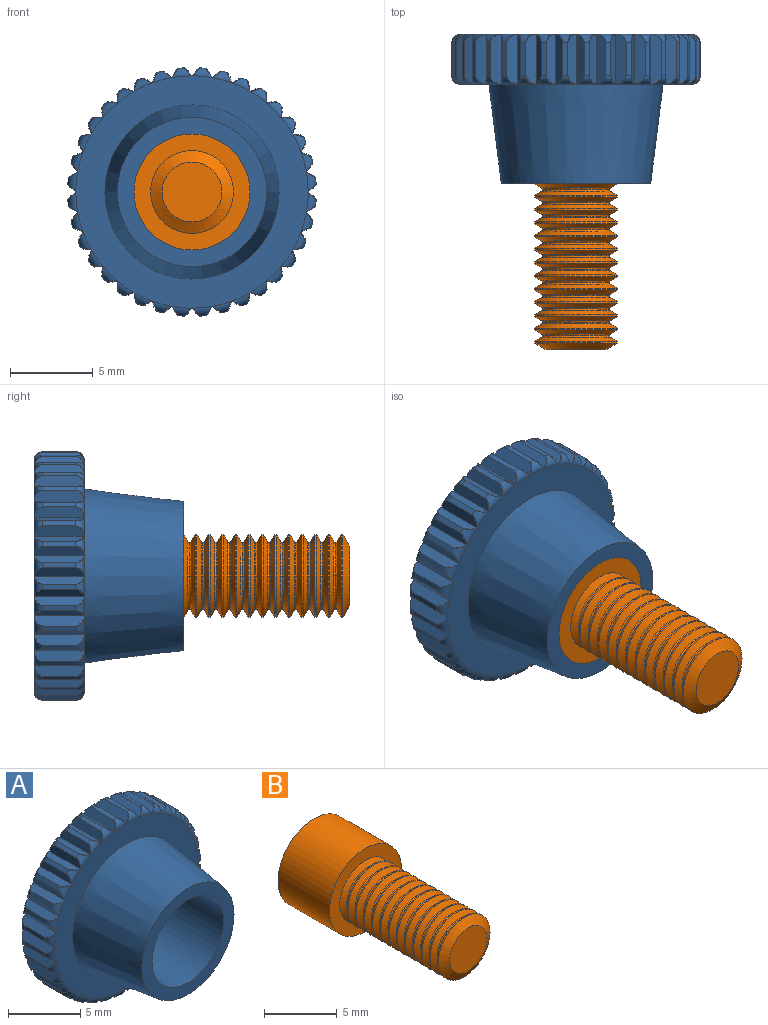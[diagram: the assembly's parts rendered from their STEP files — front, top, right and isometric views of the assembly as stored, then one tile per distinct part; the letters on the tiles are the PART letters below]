
ASSEMBLY  parts=2 mates=1
PART A: 188 faces, bbox 15.2x9.2x15.2 mm
  f0: plane 10.5x10.5mm, normal (0,1,0), area 86.6mm2, adj f1
  f1: cylinder r=5.25mm len=10.5mm, axis (0,-1,0), area 9.9mm2, adj f0,f2
  f2: plane 14x14mm, normal (0,1,0), area 67.3mm2, adj f1,f3,f4,f5,f6,f7,f8,f9
  f3: torus R=7mm, axis (0,1,0), area 0.6mm2, adj f2,f39,f40,f41
  f4: torus R=7mm, axis (0,1,0), area 0.6mm2, adj f2,f42,f43,f44
  f5: torus R=7mm, axis (0,1,0), area 0.6mm2, adj f2,f45,f46,f47
  f6: torus R=7mm, axis (0,1,0), area 0.6mm2, adj f2,f48,f49,f50
  f7: torus R=7mm, axis (0,1,0), area 0.6mm2, adj f2,f51,f52,f53
  f8: torus R=7mm, axis (0,1,0), area 0.6mm2, adj f2,f54,f55,f56
  f9: torus R=7mm, axis (0,1,0), area 0.6mm2, adj f2,f57,f58,f59
  f10: torus R=7mm, axis (0,1,0), area 0.6mm2, adj f2,f60,f61,f62
  f11: torus R=7mm, axis (0,1,0), area 0.6mm2, adj f2,f63,f64,f65
  f12: torus R=7mm, axis (0,1,0), area 0.6mm2, adj f2,f66,f67,f68
  f13: torus R=7mm, axis (0,1,0), area 0.6mm2, adj f2,f69,f70,f71
  f14: torus R=7mm, axis (0,1,0), area 0.6mm2, adj f2,f72,f73,f74
  f15: torus R=7mm, axis (0,1,0), area 0.6mm2, adj f2,f75,f76,f77
  f16: torus R=7mm, axis (0,1,0), area 0.6mm2, adj f2,f78,f79,f80
  f17: torus R=7mm, axis (0,1,0), area 0.6mm2, adj f2,f81,f82,f83
  f18: torus R=7mm, axis (0,1,0), area 0.6mm2, adj f2,f84,f85,f86
  f19: torus R=7mm, axis (0,1,0), area 0.6mm2, adj f2,f87,f88,f89
  f20: torus R=7mm, axis (0,1,0), area 0.6mm2, adj f2,f90,f91,f92
  f21: torus R=7mm, axis (0,1,0), area 0.6mm2, adj f2,f93,f94,f95
  f22: torus R=7mm, axis (0,1,0), area 0.6mm2, adj f2,f96,f97,f98
  f23: torus R=7mm, axis (0,1,0), area 0.6mm2, adj f2,f99,f100,f101
  f24: torus R=7mm, axis (0,1,0), area 0.6mm2, adj f2,f102,f103,f104
  f25: torus R=7mm, axis (0,1,0), area 0.6mm2, adj f2,f105,f106,f107
  f26: torus R=7mm, axis (0,1,0), area 0.6mm2, adj f2,f108,f109,f110
  f27: torus R=7mm, axis (0,1,0), area 0.6mm2, adj f2,f111,f112,f113
  f28: torus R=7mm, axis (0,1,0), area 0.6mm2, adj f2,f114,f115,f116
  f29: torus R=7mm, axis (0,1,0), area 0.6mm2, adj f2,f117,f118,f119
  f30: torus R=7mm, axis (0,1,0), area 0.6mm2, adj f2,f120,f121,f122
  f31: torus R=7mm, axis (0,1,0), area 0.6mm2, adj f2,f123,f124,f125
  f32: torus R=7mm, axis (0,1,0), area 0.6mm2, adj f2,f126,f127,f128
  f33: torus R=7mm, axis (0,1,0), area 0.6mm2, adj f2,f129,f130,f131
  f34: torus R=7mm, axis (0,1,0), area 0.6mm2, adj f2,f132,f133,f134
  f35: torus R=7mm, axis (0,1,0), area 0.6mm2, adj f2,f135,f136,f137
  f36: torus R=7mm, axis (0,1,0), area 0.6mm2, adj f2,f138,f139,f140
  f37: torus R=7mm, axis (0,1,0), area 0.6mm2, adj f2,f141,f142,f143
  f38: torus R=7mm, axis (0,1,0), area 0.6mm2, adj f2,f144,f145,f146
  f39: plane 3.19x0.75mm, normal (-0.57,0,-0.82), area 1.9mm2, adj f3,f41,f42,f147
  f40: plane 3.19x0.67mm, normal (-0.71,0,0.71), area 1.9mm2, adj f3,f41,f146,f147
  f41: cylinder r=7.5mm len=2mm, axis (0,-1,0), area 0.7mm2, adj f3,f39,f40,f147
  f42: plane 3.19x0.75mm, normal (-0.82,0,0.57), area 1.9mm2, adj f4,f39,f43,f148
  f43: cylinder r=7.5mm len=2mm, axis (0,-1,0), area 0.7mm2, adj f4,f42,f44,f148
  f44: plane 3.19x0.81mm, normal (-0.42,0,-0.91), area 1.9mm2, adj f4,f43,f45,f148
  f45: plane 3.19x0.81mm, normal (-0.91,0,0.42), area 1.9mm2, adj f5,f44,f46,f149
  f46: cylinder r=7.5mm len=2mm, axis (0,-1,0), area 0.7mm2, adj f5,f45,f47,f149
  f47: plane 3.19x0.85mm, normal (-0.26,0,-0.97), area 1.9mm2, adj f5,f46,f48,f149
  f48: plane 3.19x0.85mm, normal (-0.97,0,0.26), area 1.9mm2, adj f6,f47,f49,f150
  f49: cylinder r=7.5mm len=2mm, axis (0,-1,0), area 0.7mm2, adj f6,f48,f50,f150
  f50: plane 3.19x0.87mm, normal (-0.09,0,-1), area 1.9mm2, adj f6,f49,f51,f150
  f51: plane 3.19x0.87mm, normal (-1,0,0.09), area 1.9mm2, adj f7,f50,f52,f151
  f52: cylinder r=7.5mm len=2mm, axis (0,-1,0), area 0.7mm2, adj f7,f51,f53,f151
  f53: plane 3.19x0.87mm, normal (0.09,0,-1), area 1.9mm2, adj f7,f52,f54,f151
  f54: plane 3.19x0.87mm, normal (-1,0,-0.09), area 1.9mm2, adj f8,f53,f55,f152
  f55: cylinder r=7.5mm len=2mm, axis (0,-1,0), area 0.7mm2, adj f8,f54,f56,f152
  f56: plane 3.19x0.85mm, normal (0.26,0,-0.97), area 1.9mm2, adj f8,f55,f57,f152
  f57: plane 3.19x0.85mm, normal (-0.97,0,-0.26), area 1.9mm2, adj f9,f56,f58,f153
  f58: cylinder r=7.5mm len=2mm, axis (0,-1,0), area 0.7mm2, adj f9,f57,f59,f153
  f59: plane 3.19x0.81mm, normal (0.42,0,-0.91), area 1.9mm2, adj f9,f58,f60,f153
  f60: plane 3.19x0.81mm, normal (-0.91,0,-0.42), area 1.9mm2, adj f10,f59,f61,f154
  f61: cylinder r=7.5mm len=2mm, axis (0,-1,0), area 0.7mm2, adj f10,f60,f62,f154
  f62: plane 3.19x0.75mm, normal (0.57,0,-0.82), area 1.9mm2, adj f10,f61,f63,f154
  f63: plane 3.19x0.75mm, normal (-0.82,0,-0.57), area 1.9mm2, adj f11,f62,f64,f155
  f64: cylinder r=7.5mm len=2mm, axis (0,-1,0), area 0.7mm2, adj f11,f63,f65,f155
  f65: plane 3.19x0.67mm, normal (0.71,0,-0.71), area 1.9mm2, adj f11,f64,f66,f155
  f66: plane 3.19x0.67mm, normal (-0.71,0,-0.71), area 1.9mm2, adj f12,f65,f67,f156
  f67: cylinder r=7.5mm len=2mm, axis (0,-1,0), area 0.7mm2, adj f12,f66,f68,f156
  f68: plane 3.19x0.75mm, normal (0.82,0,-0.57), area 1.9mm2, adj f12,f67,f69,f156
  f69: plane 3.19x0.75mm, normal (-0.57,0,-0.82), area 1.9mm2, adj f13,f68,f70,f157
  f70: cylinder r=7.5mm len=2mm, axis (0,-1,0), area 0.7mm2, adj f13,f69,f71,f157
  f71: plane 3.19x0.81mm, normal (0.91,0,-0.42), area 1.9mm2, adj f13,f70,f72,f157
  f72: plane 3.19x0.81mm, normal (-0.42,0,-0.91), area 1.9mm2, adj f14,f71,f73,f158
  f73: cylinder r=7.5mm len=2mm, axis (0,-1,0), area 0.7mm2, adj f14,f72,f74,f158
  f74: plane 3.19x0.85mm, normal (0.97,0,-0.26), area 1.9mm2, adj f14,f73,f75,f158
  f75: plane 3.19x0.85mm, normal (-0.26,0,-0.97), area 1.9mm2, adj f15,f74,f76,f159
  f76: cylinder r=7.5mm len=2mm, axis (0,-1,0), area 0.7mm2, adj f15,f75,f77,f159
  f77: plane 3.19x0.87mm, normal (1,0,-0.09), area 1.9mm2, adj f15,f76,f78,f159
  f78: plane 3.19x0.87mm, normal (-0.09,0,-1), area 1.9mm2, adj f16,f77,f79,f160
  f79: cylinder r=7.5mm len=2mm, axis (0,-1,0), area 0.7mm2, adj f16,f78,f80,f160
  f80: plane 3.19x0.87mm, normal (1,0,0.09), area 1.9mm2, adj f16,f79,f81,f160
  f81: plane 3.19x0.87mm, normal (0.09,0,-1), area 1.9mm2, adj f17,f80,f82,f161
  f82: cylinder r=7.5mm len=2mm, axis (0,-1,0), area 0.7mm2, adj f17,f81,f83,f161
  f83: plane 3.19x0.85mm, normal (0.97,0,0.26), area 1.9mm2, adj f17,f82,f84,f161
  f84: plane 3.19x0.85mm, normal (0.26,0,-0.97), area 1.9mm2, adj f18,f83,f85,f162
  f85: cylinder r=7.5mm len=2mm, axis (0,-1,0), area 0.7mm2, adj f18,f84,f86,f162
  f86: plane 3.19x0.81mm, normal (0.91,0,0.42), area 1.9mm2, adj f18,f85,f87,f162
  f87: plane 3.19x0.81mm, normal (0.42,0,-0.91), area 1.9mm2, adj f19,f86,f88,f163
  f88: cylinder r=7.5mm len=2mm, axis (0,-1,0), area 0.7mm2, adj f19,f87,f89,f163
  f89: plane 3.19x0.75mm, normal (0.82,0,0.57), area 1.9mm2, adj f19,f88,f90,f163
  f90: plane 3.19x0.75mm, normal (0.57,0,-0.82), area 1.9mm2, adj f20,f89,f91,f164
  f91: cylinder r=7.5mm len=2mm, axis (0,-1,0), area 0.7mm2, adj f20,f90,f92,f164
  f92: plane 3.19x0.67mm, normal (0.71,0,0.71), area 1.9mm2, adj f20,f91,f93,f164
  f93: plane 3.19x0.67mm, normal (0.71,0,-0.71), area 1.9mm2, adj f21,f92,f94,f165
  f94: cylinder r=7.5mm len=2mm, axis (0,-1,0), area 0.7mm2, adj f21,f93,f95,f165
  f95: plane 3.19x0.75mm, normal (0.57,0,0.82), area 1.9mm2, adj f21,f94,f96,f165
  f96: plane 3.19x0.75mm, normal (0.82,0,-0.57), area 1.9mm2, adj f22,f95,f97,f166
  f97: cylinder r=7.5mm len=2mm, axis (0,-1,0), area 0.7mm2, adj f22,f96,f98,f166
  f98: plane 3.19x0.81mm, normal (0.42,0,0.91), area 1.9mm2, adj f22,f97,f99,f166
  f99: plane 3.19x0.81mm, normal (0.91,0,-0.42), area 1.9mm2, adj f23,f98,f100,f167
  f100: cylinder r=7.5mm len=2mm, axis (0,-1,0), area 0.7mm2, adj f23,f99,f101,f167
  f101: plane 3.19x0.85mm, normal (0.26,0,0.97), area 1.9mm2, adj f23,f100,f102,f167
  f102: plane 3.19x0.85mm, normal (0.97,0,-0.26), area 1.9mm2, adj f24,f101,f103,f168
  f103: cylinder r=7.5mm len=2mm, axis (0,-1,0), area 0.7mm2, adj f24,f102,f104,f168
  f104: plane 3.19x0.87mm, normal (0.09,0,1), area 1.9mm2, adj f24,f103,f105,f168
  f105: plane 3.19x0.87mm, normal (1,0,-0.09), area 1.9mm2, adj f25,f104,f106,f169
  f106: cylinder r=7.5mm len=2mm, axis (0,-1,0), area 0.7mm2, adj f25,f105,f107,f169
  f107: plane 3.19x0.87mm, normal (-0.09,0,1), area 1.9mm2, adj f25,f106,f108,f169
  f108: plane 3.19x0.87mm, normal (1,0,0.09), area 1.9mm2, adj f26,f107,f109,f170
  f109: cylinder r=7.5mm len=2mm, axis (0,-1,0), area 0.7mm2, adj f26,f108,f110,f170
  f110: plane 3.19x0.85mm, normal (-0.26,0,0.97), area 1.9mm2, adj f26,f109,f111,f170
  f111: plane 3.19x0.85mm, normal (0.97,0,0.26), area 1.9mm2, adj f27,f110,f112,f171
  f112: cylinder r=7.5mm len=2mm, axis (0,-1,0), area 0.7mm2, adj f27,f111,f113,f171
  f113: plane 3.19x0.81mm, normal (-0.42,0,0.91), area 1.9mm2, adj f27,f112,f114,f171
  f114: plane 3.19x0.81mm, normal (0.91,0,0.42), area 1.9mm2, adj f28,f113,f115,f172
  f115: cylinder r=7.5mm len=2mm, axis (0,-1,0), area 0.7mm2, adj f28,f114,f116,f172
  f116: plane 3.19x0.75mm, normal (-0.57,0,0.82), area 1.9mm2, adj f28,f115,f117,f172
  f117: plane 3.19x0.75mm, normal (0.82,0,0.57), area 1.9mm2, adj f29,f116,f118,f173
  f118: cylinder r=7.5mm len=2mm, axis (0,-1,0), area 0.7mm2, adj f29,f117,f119,f173
  f119: plane 3.19x0.67mm, normal (-0.71,0,0.71), area 1.9mm2, adj f29,f118,f120,f173
  f120: plane 3.19x0.67mm, normal (0.71,0,0.71), area 1.9mm2, adj f30,f119,f121,f174
  f121: cylinder r=7.5mm len=2mm, axis (0,-1,0), area 0.7mm2, adj f30,f120,f122,f174
  f122: plane 3.19x0.75mm, normal (-0.82,0,0.57), area 1.9mm2, adj f30,f121,f123,f174
  f123: plane 3.19x0.75mm, normal (0.57,0,0.82), area 1.9mm2, adj f31,f122,f124,f175
  f124: cylinder r=7.5mm len=2mm, axis (0,-1,0), area 0.7mm2, adj f31,f123,f125,f175
  f125: plane 3.19x0.81mm, normal (-0.91,0,0.42), area 1.9mm2, adj f31,f124,f126,f175
  f126: plane 3.19x0.81mm, normal (0.42,0,0.91), area 1.9mm2, adj f32,f125,f127,f176
  f127: cylinder r=7.5mm len=2mm, axis (0,-1,0), area 0.7mm2, adj f32,f126,f128,f176
  f128: plane 3.19x0.85mm, normal (-0.97,0,0.26), area 1.9mm2, adj f32,f127,f129,f176
  f129: plane 3.19x0.85mm, normal (0.26,0,0.97), area 1.9mm2, adj f33,f128,f130,f177
  f130: cylinder r=7.5mm len=2mm, axis (0,-1,0), area 0.7mm2, adj f33,f129,f131,f177
  f131: plane 3.19x0.87mm, normal (-1,0,0.09), area 1.9mm2, adj f33,f130,f132,f177
  f132: plane 3.19x0.87mm, normal (0.09,0,1), area 1.9mm2, adj f34,f131,f133,f178
  f133: cylinder r=7.5mm len=2mm, axis (0,-1,0), area 0.7mm2, adj f34,f132,f134,f178
  f134: plane 3.19x0.87mm, normal (-1,0,-0.09), area 1.9mm2, adj f34,f133,f135,f178
  f135: plane 3.19x0.87mm, normal (-0.09,0,1), area 1.9mm2, adj f35,f134,f136,f179
  f136: cylinder r=7.5mm len=2mm, axis (0,-1,0), area 0.7mm2, adj f35,f135,f137,f179
  f137: plane 3.19x0.85mm, normal (-0.97,0,-0.26), area 1.9mm2, adj f35,f136,f138,f179
  f138: plane 3.19x0.85mm, normal (-0.26,0,0.97), area 1.9mm2, adj f36,f137,f139,f180
  f139: cylinder r=7.5mm len=2mm, axis (0,-1,0), area 0.7mm2, adj f36,f138,f140,f180
  f140: plane 3.19x0.81mm, normal (-0.91,0,-0.42), area 1.9mm2, adj f36,f139,f141,f180
  f141: plane 3.19x0.81mm, normal (-0.42,0,0.91), area 1.9mm2, adj f37,f140,f142,f181
  f142: cylinder r=7.5mm len=2mm, axis (0,-1,0), area 0.7mm2, adj f37,f141,f143,f181
  f143: plane 3.19x0.75mm, normal (-0.82,0,-0.57), area 1.9mm2, adj f37,f142,f144,f181
  f144: plane 3.19x0.75mm, normal (-0.57,0,0.82), area 1.9mm2, adj f38,f143,f145,f182
  f145: cylinder r=7.5mm len=2mm, axis (0,-1,0), area 0.7mm2, adj f38,f144,f146,f182
  f146: plane 3.19x0.67mm, normal (-0.71,0,-0.71), area 1.9mm2, adj f38,f40,f145,f182
  f147: torus R=7mm, axis (0,-1,0), area 0.6mm2, adj f39,f40,f41,f183
  f148: torus R=7mm, axis (0,-1,0), area 0.6mm2, adj f42,f43,f44,f183
  f149: torus R=7mm, axis (0,-1,0), area 0.6mm2, adj f45,f46,f47,f183
  f150: torus R=7mm, axis (0,-1,0), area 0.6mm2, adj f48,f49,f50,f183
  f151: torus R=7mm, axis (0,-1,0), area 0.6mm2, adj f51,f52,f53,f183
  f152: torus R=7mm, axis (0,-1,0), area 0.6mm2, adj f54,f55,f56,f183
  f153: torus R=7mm, axis (0,-1,0), area 0.6mm2, adj f57,f58,f59,f183
  f154: torus R=7mm, axis (0,-1,0), area 0.6mm2, adj f60,f61,f62,f183
  f155: torus R=7mm, axis (0,-1,0), area 0.6mm2, adj f63,f64,f65,f183
  f156: torus R=7mm, axis (0,-1,0), area 0.6mm2, adj f66,f67,f68,f183
  f157: torus R=7mm, axis (0,-1,0), area 0.6mm2, adj f69,f70,f71,f183
  f158: torus R=7mm, axis (0,-1,0), area 0.6mm2, adj f72,f73,f74,f183
  f159: torus R=7mm, axis (0,-1,0), area 0.6mm2, adj f75,f76,f77,f183
  f160: torus R=7mm, axis (0,-1,0), area 0.6mm2, adj f78,f79,f80,f183
  f161: torus R=7mm, axis (0,-1,0), area 0.6mm2, adj f81,f82,f83,f183
  f162: torus R=7mm, axis (0,-1,0), area 0.6mm2, adj f84,f85,f86,f183
  f163: torus R=7mm, axis (0,-1,0), area 0.6mm2, adj f87,f88,f89,f183
  f164: torus R=7mm, axis (0,-1,0), area 0.6mm2, adj f90,f91,f92,f183
  f165: torus R=7mm, axis (0,-1,0), area 0.6mm2, adj f93,f94,f95,f183
  f166: torus R=7mm, axis (0,-1,0), area 0.6mm2, adj f96,f97,f98,f183
  f167: torus R=7mm, axis (0,-1,0), area 0.6mm2, adj f99,f100,f101,f183
  f168: torus R=7mm, axis (0,-1,0), area 0.6mm2, adj f102,f103,f104,f183
  f169: torus R=7mm, axis (0,-1,0), area 0.6mm2, adj f105,f106,f107,f183
  f170: torus R=7mm, axis (0,-1,0), area 0.6mm2, adj f108,f109,f110,f183
  f171: torus R=7mm, axis (0,-1,0), area 0.6mm2, adj f111,f112,f113,f183
  f172: torus R=7mm, axis (0,-1,0), area 0.6mm2, adj f114,f115,f116,f183
  f173: torus R=7mm, axis (0,-1,0), area 0.6mm2, adj f117,f118,f119,f183
  f174: torus R=7mm, axis (0,-1,0), area 0.6mm2, adj f120,f121,f122,f183
  f175: torus R=7mm, axis (0,-1,0), area 0.6mm2, adj f123,f124,f125,f183
  f176: torus R=7mm, axis (0,-1,0), area 0.6mm2, adj f126,f127,f128,f183
  f177: torus R=7mm, axis (0,-1,0), area 0.6mm2, adj f129,f130,f131,f183
  f178: torus R=7mm, axis (0,-1,0), area 0.6mm2, adj f132,f133,f134,f183
  f179: torus R=7mm, axis (0,-1,0), area 0.6mm2, adj f135,f136,f137,f183
  f180: torus R=7mm, axis (0,-1,0), area 0.6mm2, adj f138,f139,f140,f183
  f181: torus R=7mm, axis (0,-1,0), area 0.6mm2, adj f141,f142,f143,f183
  f182: torus R=7mm, axis (0,-1,0), area 0.6mm2, adj f144,f145,f146,f183
  f183: plane 14x14mm, normal (0,-1,0), area 67.3mm2, adj f147,f148,f149,f150,f151,f152,f153,f154
  f184: cone r=0mm half-angle=7.1deg, axis (0,1,0), area 185.2mm2, adj f183,f186
  f185: plane 7x7mm, normal (0,-1,0), area 38.5mm2, adj f187
  f186: plane 9x9mm, normal (0,-1,0), area 25.1mm2, adj f184,f187
  f187: cylinder r=3.5mm len=7mm, axis (0,-1,0), area 110mm2, adj f185,f186
PART B: 89 faces, bbox 7x15x7 mm
  f0: plane 7x7mm, normal (0,1,0), area 38.5mm2, adj f1
  f1: cylinder r=3.5mm len=7mm, axis (0,-1,0), area 110mm2, adj f0,f2
  f2: plane 7x7mm, normal (0,-1,0), area 18.8mm2, adj f1,f3
  f3: cone r=0mm half-angle=60deg, axis (0,1,0), area 7.2mm2, adj f2,f4,f5
  f4: torus R=2.12mm, axis (0,1,0), area 0.8mm2, adj f3,f5,f6
  f5: torus R=2.12mm, axis (0,1,0), area 0.8mm2, adj f3,f4,f7
  f6: torus R=2.12mm, axis (0,1,0), area 0.8mm2, adj f4,f7,f8
  f7: torus R=2.12mm, axis (0,1,0), area 0.8mm2, adj f5,f6,f8
  f8: cone r=0mm half-angle=60deg, axis (0,-1,0), area 7.2mm2, adj f6,f7,f9
  f9: cylinder r=2.5mm len=5mm, axis (0,1,0), area 1.6mm2, adj f8,f10
  f10: cone r=0mm half-angle=60deg, axis (0,1,0), area 7.2mm2, adj f9,f11,f12
  f11: torus R=2.12mm, axis (0,1,0), area 0.8mm2, adj f10,f12,f13
  f12: torus R=2.12mm, axis (0,1,0), area 0.8mm2, adj f10,f11,f14
  f13: torus R=2.12mm, axis (0,1,0), area 0.8mm2, adj f11,f14,f15
  f14: torus R=2.12mm, axis (0,1,0), area 0.8mm2, adj f12,f13,f15
  f15: cone r=0mm half-angle=60deg, axis (0,-1,0), area 7.2mm2, adj f13,f14,f16
  f16: cylinder r=2.5mm len=5mm, axis (0,1,0), area 1.6mm2, adj f15,f17
  f17: cone r=0mm half-angle=60deg, axis (0,1,0), area 7.2mm2, adj f16,f18,f19
  f18: torus R=2.12mm, axis (0,1,0), area 0.8mm2, adj f17,f19,f20
  f19: torus R=2.12mm, axis (0,1,0), area 0.8mm2, adj f17,f18,f21
  f20: torus R=2.12mm, axis (0,1,0), area 0.8mm2, adj f18,f21,f22
  f21: torus R=2.12mm, axis (0,1,0), area 0.8mm2, adj f19,f20,f22
  f22: cone r=0mm half-angle=60deg, axis (0,-1,0), area 7.2mm2, adj f20,f21,f23
  f23: cylinder r=2.5mm len=5mm, axis (0,1,0), area 1.6mm2, adj f22,f24
  f24: cone r=0mm half-angle=60deg, axis (0,1,0), area 7.2mm2, adj f23,f25,f26
  f25: torus R=2.12mm, axis (0,1,0), area 0.8mm2, adj f24,f26,f27
  f26: torus R=2.12mm, axis (0,1,0), area 0.8mm2, adj f24,f25,f28
  f27: torus R=2.12mm, axis (0,1,0), area 0.8mm2, adj f25,f28,f29
  f28: torus R=2.12mm, axis (0,1,0), area 0.8mm2, adj f26,f27,f29
  f29: cone r=0mm half-angle=60deg, axis (0,-1,0), area 7.2mm2, adj f27,f28,f30
  f30: cylinder r=2.5mm len=5mm, axis (0,1,0), area 1.6mm2, adj f29,f31
  f31: cone r=0mm half-angle=60deg, axis (0,1,0), area 7.2mm2, adj f30,f32,f33
  f32: torus R=2.12mm, axis (0,1,0), area 0.8mm2, adj f31,f33,f34
  f33: torus R=2.12mm, axis (0,1,0), area 0.8mm2, adj f31,f32,f35
  f34: torus R=2.12mm, axis (0,1,0), area 0.8mm2, adj f32,f35,f36
  f35: torus R=2.12mm, axis (0,1,0), area 0.8mm2, adj f33,f34,f36
  f36: cone r=0mm half-angle=60deg, axis (0,-1,0), area 7.2mm2, adj f34,f35,f37
  f37: cylinder r=2.5mm len=5mm, axis (0,1,0), area 1.6mm2, adj f36,f38
  f38: cone r=0mm half-angle=60deg, axis (0,1,0), area 7.2mm2, adj f37,f39,f40
  f39: torus R=2.12mm, axis (0,1,0), area 0.8mm2, adj f38,f40,f41
  f40: torus R=2.12mm, axis (0,1,0), area 0.8mm2, adj f38,f39,f42
  f41: torus R=2.12mm, axis (0,1,0), area 0.8mm2, adj f39,f42,f43
  f42: torus R=2.12mm, axis (0,1,0), area 0.8mm2, adj f40,f41,f43
  f43: cone r=0mm half-angle=60deg, axis (0,-1,0), area 7.2mm2, adj f41,f42,f44
  f44: cylinder r=2.5mm len=5mm, axis (0,1,0), area 1.6mm2, adj f43,f45
  f45: cone r=0mm half-angle=60deg, axis (0,1,0), area 7.2mm2, adj f44,f46,f47
  f46: torus R=2.12mm, axis (0,1,0), area 0.8mm2, adj f45,f47,f48
  f47: torus R=2.12mm, axis (0,1,0), area 0.8mm2, adj f45,f46,f49
  f48: torus R=2.12mm, axis (0,1,0), area 0.8mm2, adj f46,f49,f50
  f49: torus R=2.12mm, axis (0,1,0), area 0.8mm2, adj f47,f48,f50
  f50: cone r=0mm half-angle=60deg, axis (0,-1,0), area 7.2mm2, adj f48,f49,f51
  f51: cylinder r=2.5mm len=5mm, axis (0,1,0), area 1.6mm2, adj f50,f52
  f52: cone r=0mm half-angle=60deg, axis (0,1,0), area 7.2mm2, adj f51,f53,f54
  f53: torus R=2.12mm, axis (0,1,0), area 0.8mm2, adj f52,f54,f55
  f54: torus R=2.12mm, axis (0,1,0), area 0.8mm2, adj f52,f53,f56
  f55: torus R=2.12mm, axis (0,1,0), area 0.8mm2, adj f53,f56,f57
  f56: torus R=2.12mm, axis (0,1,0), area 0.8mm2, adj f54,f55,f57
  f57: cone r=0mm half-angle=60deg, axis (0,-1,0), area 7.2mm2, adj f55,f56,f58
  f58: cylinder r=2.5mm len=5mm, axis (0,1,0), area 1.6mm2, adj f57,f59
  f59: cone r=0mm half-angle=60deg, axis (0,1,0), area 7.2mm2, adj f58,f60,f61
  f60: torus R=2.12mm, axis (0,1,0), area 0.8mm2, adj f59,f61,f62
  f61: torus R=2.12mm, axis (0,1,0), area 0.8mm2, adj f59,f60,f63
  f62: torus R=2.12mm, axis (0,1,0), area 0.8mm2, adj f60,f63,f64
  f63: torus R=2.12mm, axis (0,1,0), area 0.8mm2, adj f61,f62,f64
  f64: cone r=0mm half-angle=60deg, axis (0,-1,0), area 7.2mm2, adj f62,f63,f65
  f65: cylinder r=2.5mm len=5mm, axis (0,1,0), area 1.6mm2, adj f64,f66
  f66: cone r=0mm half-angle=60deg, axis (0,1,0), area 7.2mm2, adj f65,f67,f68
  f67: torus R=2.12mm, axis (0,1,0), area 0.8mm2, adj f66,f68,f69
  f68: torus R=2.12mm, axis (0,1,0), area 0.8mm2, adj f66,f67,f70
  f69: torus R=2.12mm, axis (0,1,0), area 0.8mm2, adj f67,f70,f71
  f70: torus R=2.12mm, axis (0,1,0), area 0.8mm2, adj f68,f69,f71
  f71: cone r=0mm half-angle=60deg, axis (0,-1,0), area 7.2mm2, adj f69,f70,f72
  f72: cylinder r=2.5mm len=5mm, axis (0,1,0), area 1.6mm2, adj f71,f73
  f73: cone r=0mm half-angle=60deg, axis (0,1,0), area 7.2mm2, adj f72,f74,f75
  f74: torus R=2.12mm, axis (0,1,0), area 0.8mm2, adj f73,f75,f76
  f75: torus R=2.12mm, axis (0,1,0), area 0.8mm2, adj f73,f74,f78
  f76: torus R=2.12mm, axis (0,1,0), area 0.8mm2, adj f74,f78,f81
  f77: plane 3.61x3.61mm, normal (0,-1,0), area 10.3mm2, adj f79
  f78: torus R=2.12mm, axis (0,1,0), area 0.8mm2, adj f75,f76,f81
  f79: cone r=0mm half-angle=60deg, axis (0,1,0), area 10.8mm2, adj f77,f83
  f80: torus R=2.12mm, axis (0,1,0), area 0.8mm2, adj f82,f85,f87
  f81: cone r=0mm half-angle=60deg, axis (0,-1,0), area 7.2mm2, adj f76,f78,f84
  f82: torus R=2.12mm, axis (0,1,0), area 0.8mm2, adj f80,f86,f88
  f83: cylinder r=2.5mm len=5mm, axis (0,1,0), area 1.6mm2, adj f79,f85
  f84: cylinder r=2.5mm len=5mm, axis (0,1,0), area 1.6mm2, adj f81,f86
  f85: cone r=0mm half-angle=60deg, axis (0,-1,0), area 7.2mm2, adj f80,f83,f87
  f86: cone r=0mm half-angle=60deg, axis (0,1,0), area 7.2mm2, adj f82,f84,f88
  f87: torus R=2.12mm, axis (0,1,0), area 0.8mm2, adj f80,f85,f88
  f88: torus R=2.12mm, axis (0,1,0), area 0.8mm2, adj f82,f86,f87
PLACE A t=(0,4.8,0)mm
PLACE B t=(0,4.8,0)mm
MATE fastened B.f1 <-> A.f1  axis (0,-1,0) through (0,9.8,0)mm
